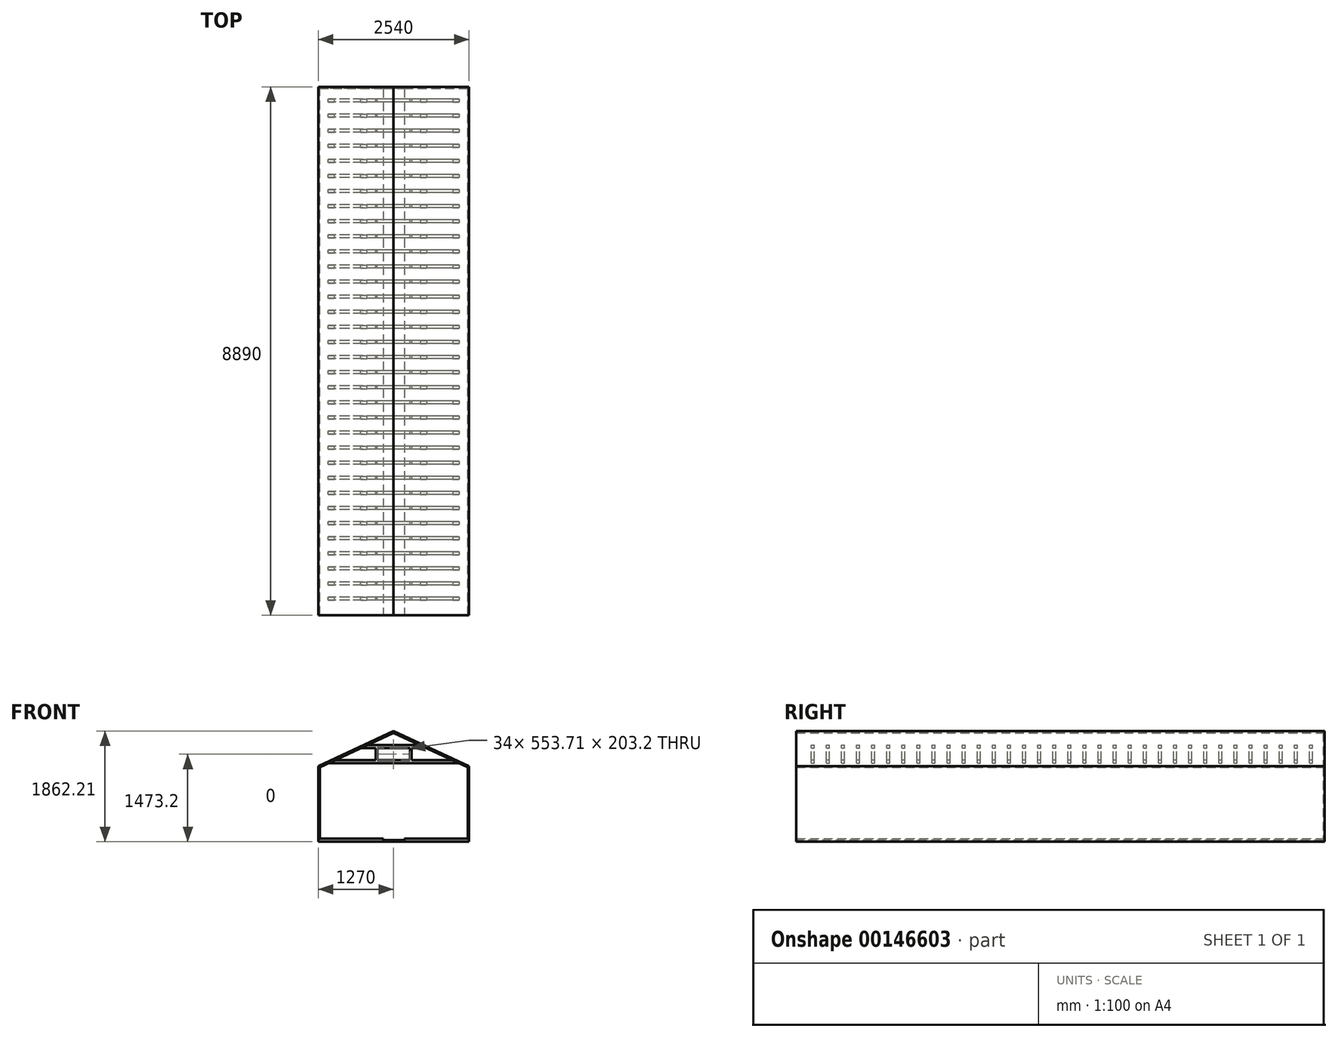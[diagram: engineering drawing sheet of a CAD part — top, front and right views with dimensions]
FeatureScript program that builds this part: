
annotation { "Feature Type Name" : "Feature", "Feature Type Description" : "" }
export const myFeature = defineFeature(function(context is Context, id is Id, definition is map)
    precondition{}
    {
        {
            var Q0;
            Q0=qCreatedBy(makeId("Front.planeOp"),FACE);
            var sketch = newSketch(context, id + "F0", { "sketchPlane" : qUnion([Q0])});
            skLineSegment(sketch, "E0", {"start": v(-1270, 1270) * mm, "end": v(-1270, 0) * mm});
            skLineSegment(sketch, "E1", {"start": v(-1270, 0) * mm, "end": v(1270, 0) * mm});
            skLineSegment(sketch, "E2", {"start": v(1270, 0) * mm, "end": v(1270, 1270) * mm});
            skLineSegment(sketch, "E3", {"start": v(1270, 1270) * mm, "end": v(0, 1862.21) * mm});
            skLineSegment(sketch, "E4", {"start": v(0, 1862.21) * mm, "end": v(-1270, 1270) * mm});
            skSolve(sketch);
        }
        {
            var Q0;
            Q0 = qSketchRegion(id + "F0", true);
            extrude(context, id + "F1", {"entities" : qUnion([Q0]), "depth" : 8890 * mm});
        }
        {
            var Q0;
            Q0=makeQuery(id+"F1.opExtrude","CAP_FACE",FACE,{"disambiguationData":[OSD([sQuery(id+"F0.wireOp",EDGE,"E0"),sQuery(id+"F0.wireOp",EDGE,"E1"),sQuery(id+"F0.wireOp",EDGE,"E2"),sQuery(id+"F0.wireOp",EDGE,"E3"),sQuery(id+"F0.wireOp",EDGE,"E4")])],"isStart":false});
            shell(context, id + "F2", {"entities" : qUnion([Q0]), "thickness" : 25.4 * mm});
        }
        {
            var Q0;
            Q0=makeQuery(id+"F2.opShell","OFFSET_FACE",FACE,{"disambiguationData":[OSD([sQuery(id+"F0.wireOp",EDGE,"E1")])]});
            var sketch = newSketch(context, id + "F3", { "sketchPlane" : qUnion([Q0])});
            skLineSegment(sketch, "E5.bottom", {"start": v(-1244.6, -25.4) * mm, "end": v(1244.6, -25.4) * mm});
            skLineSegment(sketch, "E5.top", {"start": v(-1244.6, -8890) * mm, "end": v(1244.6, -8890) * mm});
            skLineSegment(sketch, "E5.left", {"start": v(-1244.6, -25.4) * mm, "end": v(-1244.6, -8890) * mm});
            skLineSegment(sketch, "E5.right", {"start": v(1244.6, -25.4) * mm, "end": v(1244.6, -8890) * mm});
            skLineSegment(sketch, "E6.bottom", {"start": v(-152.4, -25.4) * mm, "end": v(152.4, -25.4) * mm});
            skLineSegment(sketch, "E6.top", {"start": v(-152.4, -8890) * mm, "end": v(152.4, -8890) * mm});
            skLineSegment(sketch, "E6.left", {"start": v(-152.4, -25.4) * mm, "end": v(-152.4, -8890) * mm});
            skLineSegment(sketch, "E6.right", {"start": v(152.4, -25.4) * mm, "end": v(152.4, -8890) * mm});
            skLineSegment(sketch, "E7", {"start": v(-177.8, 0) * mm, "end": v(-177.8, -8890) * mm});
            skLineSegment(sketch, "E8", {"start": v(-177.8, -8890) * mm, "end": v(-152.4, -8890) * mm});
            skLineSegment(sketch, "E9", {"start": v(-177.8, 0) * mm, "end": v(-152.4, 0) * mm});
            skLineSegment(sketch, "E10", {"start": v(-152.4, 0) * mm, "end": v(-152.4, -25.4) * mm});
            skLineSegment(sketch, "E11", {"start": v(152.4, -25.4) * mm, "end": v(152.4, 0) * mm});
            skLineSegment(sketch, "E12", {"start": v(152.4, 0) * mm, "end": v(177.8, 0) * mm});
            skLineSegment(sketch, "E13", {"start": v(177.8, 0) * mm, "end": v(177.8, -8890) * mm});
            skLineSegment(sketch, "E14", {"start": v(152.4, -8890) * mm, "end": v(177.8, -8890) * mm});
            skSolve(sketch);
        }
        {
            var Q0;
            {var subQ0=sQuery(id+"F3.wireOp",EDGE,"E5.left");Q0=makeQuery(id+"F3.imprint","IMPRINT",FACE,{"disambiguationData":[TD([[makeQuery(id+"F3.imprint","IMPRINT",EDGE,{"derivedFrom":subQ0}),-1.0]])]});}
            var Q1;
            {var subQ4=sQuery(id+"F3.wireOp",EDGE,"E9");Q1=makeQuery(id+"F3.imprint","IMPRINT",FACE,{"disambiguationData":[TD([[makeQuery(id+"F3.imprint","IMPRINT",EDGE,{"derivedFrom":subQ4}),-1.0]])]});}
            var Q2;
            {var subQ0=sQuery(id+"F3.wireOp",EDGE,"E11");Q2=makeQuery(id+"F3.imprint","IMPRINT",FACE,{"disambiguationData":[TD([[makeQuery(id+"F3.imprint","IMPRINT",EDGE,{"derivedFrom":subQ0}),-1.0]])]});}
            var Q3;
            {var subQ0=sQuery(id+"F3.wireOp",EDGE,"E5.right");Q3=makeQuery(id+"F3.imprint","IMPRINT",FACE,{"disambiguationData":[TD([[makeQuery(id+"F3.imprint","IMPRINT",EDGE,{"derivedFrom":subQ0}),1.0]])]});}
            var Q4;
            Q4=makeQuery(id+"F3.imprint","IMPRINT",FACE,{"disambiguationData":[TD([[makeQuery(id+"F3.imprint","IMPRINT",EDGE,{"derivedFrom":sQuery(id+"F3.wireOp",EDGE,"E6.bottom")}),-1.0]])]});
            extrude(context, id + "F4", {"entities" : qUnion([Q0, Q1, Q2, Q3, Q4]), "operationType" : NewBodyOperationType.ADD, "depth" : 25.4 * mm});
        }
        {
            var Q0;
            Q0=qCreatedBy(makeId("Right.planeOp"),FACE);
            var sketch = newSketch(context, id + "F5", { "sketchPlane" : qUnion([Q0])});
            skLineSegment(sketch, "E15.bottom", {"start": v(-8636, 1320.8) * mm, "end": v(-8585.2, 1320.8) * mm});
            skLineSegment(sketch, "E15.top", {"start": v(-8636, 1371.6) * mm, "end": v(-8585.2, 1371.6) * mm});
            skLineSegment(sketch, "E15.left", {"start": v(-8636, 1320.8) * mm, "end": v(-8636, 1371.6) * mm});
            skLineSegment(sketch, "E15.right", {"start": v(-8585.2, 1320.8) * mm, "end": v(-8585.2, 1371.6) * mm});
            skLineSegment(sketch, "E16.0.1.0", {"start": v(-8636, 1625.6) * mm, "end": v(-8585.2, 1625.6) * mm});
            skLineSegment(sketch, "E16.0.1.1", {"start": v(-8585.2, 1574.8) * mm, "end": v(-8585.2, 1625.6) * mm});
            skLineSegment(sketch, "E16.0.1.2", {"start": v(-8636, 1574.8) * mm, "end": v(-8585.2, 1574.8) * mm});
            skLineSegment(sketch, "E16.0.1.3", {"start": v(-8636, 1574.8) * mm, "end": v(-8636, 1625.6) * mm});
            skLineSegment(sketch, "E16.1.0.0", {"start": v(-8382, 1371.6) * mm, "end": v(-8331.2, 1371.6) * mm});
            skLineSegment(sketch, "E16.1.0.1", {"start": v(-8331.2, 1320.8) * mm, "end": v(-8331.2, 1371.6) * mm});
            skLineSegment(sketch, "E16.1.0.2", {"start": v(-8382, 1320.8) * mm, "end": v(-8331.2, 1320.8) * mm});
            skLineSegment(sketch, "E16.1.0.3", {"start": v(-8382, 1320.8) * mm, "end": v(-8382, 1371.6) * mm});
            skLineSegment(sketch, "E16.1.1.0", {"start": v(-8382, 1625.6) * mm, "end": v(-8331.2, 1625.6) * mm});
            skLineSegment(sketch, "E16.1.1.1", {"start": v(-8331.2, 1574.8) * mm, "end": v(-8331.2, 1625.6) * mm});
            skLineSegment(sketch, "E16.1.1.2", {"start": v(-8382, 1574.8) * mm, "end": v(-8331.2, 1574.8) * mm});
            skLineSegment(sketch, "E16.1.1.3", {"start": v(-8382, 1574.8) * mm, "end": v(-8382, 1625.6) * mm});
            skLineSegment(sketch, "E16.2.0.0", {"start": v(-8128, 1371.6) * mm, "end": v(-8077.2, 1371.6) * mm});
            skLineSegment(sketch, "E16.2.0.1", {"start": v(-8077.2, 1320.8) * mm, "end": v(-8077.2, 1371.6) * mm});
            skLineSegment(sketch, "E16.2.0.2", {"start": v(-8128, 1320.8) * mm, "end": v(-8077.2, 1320.8) * mm});
            skLineSegment(sketch, "E16.2.0.3", {"start": v(-8128, 1320.8) * mm, "end": v(-8128, 1371.6) * mm});
            skLineSegment(sketch, "E16.2.1.0", {"start": v(-8128, 1625.6) * mm, "end": v(-8077.2, 1625.6) * mm});
            skLineSegment(sketch, "E16.2.1.1", {"start": v(-8077.2, 1574.8) * mm, "end": v(-8077.2, 1625.6) * mm});
            skLineSegment(sketch, "E16.2.1.2", {"start": v(-8128, 1574.8) * mm, "end": v(-8077.2, 1574.8) * mm});
            skLineSegment(sketch, "E16.2.1.3", {"start": v(-8128, 1574.8) * mm, "end": v(-8128, 1625.6) * mm});
            skLineSegment(sketch, "E16.3.0.0", {"start": v(-7874, 1371.6) * mm, "end": v(-7823.2, 1371.6) * mm});
            skLineSegment(sketch, "E16.3.0.1", {"start": v(-7823.2, 1320.8) * mm, "end": v(-7823.2, 1371.6) * mm});
            skLineSegment(sketch, "E16.3.0.2", {"start": v(-7874, 1320.8) * mm, "end": v(-7823.2, 1320.8) * mm});
            skLineSegment(sketch, "E16.3.0.3", {"start": v(-7874, 1320.8) * mm, "end": v(-7874, 1371.6) * mm});
            skLineSegment(sketch, "E16.3.1.0", {"start": v(-7874, 1625.6) * mm, "end": v(-7823.2, 1625.6) * mm});
            skLineSegment(sketch, "E16.3.1.1", {"start": v(-7823.2, 1574.8) * mm, "end": v(-7823.2, 1625.6) * mm});
            skLineSegment(sketch, "E16.3.1.2", {"start": v(-7874, 1574.8) * mm, "end": v(-7823.2, 1574.8) * mm});
            skLineSegment(sketch, "E16.3.1.3", {"start": v(-7874, 1574.8) * mm, "end": v(-7874, 1625.6) * mm});
            skLineSegment(sketch, "E16.4.0.0", {"start": v(-7620, 1371.6) * mm, "end": v(-7569.2, 1371.6) * mm});
            skLineSegment(sketch, "E16.4.0.1", {"start": v(-7569.2, 1320.8) * mm, "end": v(-7569.2, 1371.6) * mm});
            skLineSegment(sketch, "E16.4.0.2", {"start": v(-7620, 1320.8) * mm, "end": v(-7569.2, 1320.8) * mm});
            skLineSegment(sketch, "E16.4.0.3", {"start": v(-7620, 1320.8) * mm, "end": v(-7620, 1371.6) * mm});
            skLineSegment(sketch, "E16.4.1.0", {"start": v(-7620, 1625.6) * mm, "end": v(-7569.2, 1625.6) * mm});
            skLineSegment(sketch, "E16.4.1.1", {"start": v(-7569.2, 1574.8) * mm, "end": v(-7569.2, 1625.6) * mm});
            skLineSegment(sketch, "E16.4.1.2", {"start": v(-7620, 1574.8) * mm, "end": v(-7569.2, 1574.8) * mm});
            skLineSegment(sketch, "E16.4.1.3", {"start": v(-7620, 1574.8) * mm, "end": v(-7620, 1625.6) * mm});
            skLineSegment(sketch, "E16.5.0.0", {"start": v(-7366, 1371.6) * mm, "end": v(-7315.2, 1371.6) * mm});
            skLineSegment(sketch, "E16.5.0.1", {"start": v(-7315.2, 1320.8) * mm, "end": v(-7315.2, 1371.6) * mm});
            skLineSegment(sketch, "E16.5.0.2", {"start": v(-7366, 1320.8) * mm, "end": v(-7315.2, 1320.8) * mm});
            skLineSegment(sketch, "E16.5.0.3", {"start": v(-7366, 1320.8) * mm, "end": v(-7366, 1371.6) * mm});
            skLineSegment(sketch, "E16.5.1.0", {"start": v(-7366, 1625.6) * mm, "end": v(-7315.2, 1625.6) * mm});
            skLineSegment(sketch, "E16.5.1.1", {"start": v(-7315.2, 1574.8) * mm, "end": v(-7315.2, 1625.6) * mm});
            skLineSegment(sketch, "E16.5.1.2", {"start": v(-7366, 1574.8) * mm, "end": v(-7315.2, 1574.8) * mm});
            skLineSegment(sketch, "E16.5.1.3", {"start": v(-7366, 1574.8) * mm, "end": v(-7366, 1625.6) * mm});
            skLineSegment(sketch, "E16.6.0.0", {"start": v(-7112, 1371.6) * mm, "end": v(-7061.2, 1371.6) * mm});
            skLineSegment(sketch, "E16.6.0.1", {"start": v(-7061.2, 1320.8) * mm, "end": v(-7061.2, 1371.6) * mm});
            skLineSegment(sketch, "E16.6.0.2", {"start": v(-7112, 1320.8) * mm, "end": v(-7061.2, 1320.8) * mm});
            skLineSegment(sketch, "E16.6.0.3", {"start": v(-7112, 1320.8) * mm, "end": v(-7112, 1371.6) * mm});
            skLineSegment(sketch, "E16.6.1.0", {"start": v(-7112, 1625.6) * mm, "end": v(-7061.2, 1625.6) * mm});
            skLineSegment(sketch, "E16.6.1.1", {"start": v(-7061.2, 1574.8) * mm, "end": v(-7061.2, 1625.6) * mm});
            skLineSegment(sketch, "E16.6.1.2", {"start": v(-7112, 1574.8) * mm, "end": v(-7061.2, 1574.8) * mm});
            skLineSegment(sketch, "E16.6.1.3", {"start": v(-7112, 1574.8) * mm, "end": v(-7112, 1625.6) * mm});
            skLineSegment(sketch, "E16.7.0.0", {"start": v(-6858, 1371.6) * mm, "end": v(-6807.2, 1371.6) * mm});
            skLineSegment(sketch, "E16.7.0.1", {"start": v(-6807.2, 1320.8) * mm, "end": v(-6807.2, 1371.6) * mm});
            skLineSegment(sketch, "E16.7.0.2", {"start": v(-6858, 1320.8) * mm, "end": v(-6807.2, 1320.8) * mm});
            skLineSegment(sketch, "E16.7.0.3", {"start": v(-6858, 1320.8) * mm, "end": v(-6858, 1371.6) * mm});
            skLineSegment(sketch, "E16.7.1.0", {"start": v(-6858, 1625.6) * mm, "end": v(-6807.2, 1625.6) * mm});
            skLineSegment(sketch, "E16.7.1.1", {"start": v(-6807.2, 1574.8) * mm, "end": v(-6807.2, 1625.6) * mm});
            skLineSegment(sketch, "E16.7.1.2", {"start": v(-6858, 1574.8) * mm, "end": v(-6807.2, 1574.8) * mm});
            skLineSegment(sketch, "E16.7.1.3", {"start": v(-6858, 1574.8) * mm, "end": v(-6858, 1625.6) * mm});
            skLineSegment(sketch, "E16.8.0.0", {"start": v(-6604, 1371.6) * mm, "end": v(-6553.2, 1371.6) * mm});
            skLineSegment(sketch, "E16.8.0.1", {"start": v(-6553.2, 1320.8) * mm, "end": v(-6553.2, 1371.6) * mm});
            skLineSegment(sketch, "E16.8.0.2", {"start": v(-6604, 1320.8) * mm, "end": v(-6553.2, 1320.8) * mm});
            skLineSegment(sketch, "E16.8.0.3", {"start": v(-6604, 1320.8) * mm, "end": v(-6604, 1371.6) * mm});
            skLineSegment(sketch, "E16.8.1.0", {"start": v(-6604, 1625.6) * mm, "end": v(-6553.2, 1625.6) * mm});
            skLineSegment(sketch, "E16.8.1.1", {"start": v(-6553.2, 1574.8) * mm, "end": v(-6553.2, 1625.6) * mm});
            skLineSegment(sketch, "E16.8.1.2", {"start": v(-6604, 1574.8) * mm, "end": v(-6553.2, 1574.8) * mm});
            skLineSegment(sketch, "E16.8.1.3", {"start": v(-6604, 1574.8) * mm, "end": v(-6604, 1625.6) * mm});
            skLineSegment(sketch, "E16.9.0.0", {"start": v(-6350, 1371.6) * mm, "end": v(-6299.2, 1371.6) * mm});
            skLineSegment(sketch, "E16.9.0.1", {"start": v(-6299.2, 1320.8) * mm, "end": v(-6299.2, 1371.6) * mm});
            skLineSegment(sketch, "E16.9.0.2", {"start": v(-6350, 1320.8) * mm, "end": v(-6299.2, 1320.8) * mm});
            skLineSegment(sketch, "E16.9.0.3", {"start": v(-6350, 1320.8) * mm, "end": v(-6350, 1371.6) * mm});
            skLineSegment(sketch, "E16.9.1.0", {"start": v(-6350, 1625.6) * mm, "end": v(-6299.2, 1625.6) * mm});
            skLineSegment(sketch, "E16.9.1.1", {"start": v(-6299.2, 1574.8) * mm, "end": v(-6299.2, 1625.6) * mm});
            skLineSegment(sketch, "E16.9.1.2", {"start": v(-6350, 1574.8) * mm, "end": v(-6299.2, 1574.8) * mm});
            skLineSegment(sketch, "E16.9.1.3", {"start": v(-6350, 1574.8) * mm, "end": v(-6350, 1625.6) * mm});
            skLineSegment(sketch, "E16.10.0.0", {"start": v(-6096, 1371.6) * mm, "end": v(-6045.2, 1371.6) * mm});
            skLineSegment(sketch, "E16.10.0.1", {"start": v(-6045.2, 1320.8) * mm, "end": v(-6045.2, 1371.6) * mm});
            skLineSegment(sketch, "E16.10.0.2", {"start": v(-6096, 1320.8) * mm, "end": v(-6045.2, 1320.8) * mm});
            skLineSegment(sketch, "E16.10.0.3", {"start": v(-6096, 1320.8) * mm, "end": v(-6096, 1371.6) * mm});
            skLineSegment(sketch, "E16.10.1.0", {"start": v(-6096, 1625.6) * mm, "end": v(-6045.2, 1625.6) * mm});
            skLineSegment(sketch, "E16.10.1.1", {"start": v(-6045.2, 1574.8) * mm, "end": v(-6045.2, 1625.6) * mm});
            skLineSegment(sketch, "E16.10.1.2", {"start": v(-6096, 1574.8) * mm, "end": v(-6045.2, 1574.8) * mm});
            skLineSegment(sketch, "E16.10.1.3", {"start": v(-6096, 1574.8) * mm, "end": v(-6096, 1625.6) * mm});
            skLineSegment(sketch, "E16.11.0.0", {"start": v(-5842, 1371.6) * mm, "end": v(-5791.2, 1371.6) * mm});
            skLineSegment(sketch, "E16.11.0.1", {"start": v(-5791.2, 1320.8) * mm, "end": v(-5791.2, 1371.6) * mm});
            skLineSegment(sketch, "E16.11.0.2", {"start": v(-5842, 1320.8) * mm, "end": v(-5791.2, 1320.8) * mm});
            skLineSegment(sketch, "E16.11.0.3", {"start": v(-5842, 1320.8) * mm, "end": v(-5842, 1371.6) * mm});
            skLineSegment(sketch, "E16.11.1.0", {"start": v(-5842, 1625.6) * mm, "end": v(-5791.2, 1625.6) * mm});
            skLineSegment(sketch, "E16.11.1.1", {"start": v(-5791.2, 1574.8) * mm, "end": v(-5791.2, 1625.6) * mm});
            skLineSegment(sketch, "E16.11.1.2", {"start": v(-5842, 1574.8) * mm, "end": v(-5791.2, 1574.8) * mm});
            skLineSegment(sketch, "E16.11.1.3", {"start": v(-5842, 1574.8) * mm, "end": v(-5842, 1625.6) * mm});
            skLineSegment(sketch, "E16.12.0.0", {"start": v(-5588, 1371.6) * mm, "end": v(-5537.2, 1371.6) * mm});
            skLineSegment(sketch, "E16.12.0.1", {"start": v(-5537.2, 1320.8) * mm, "end": v(-5537.2, 1371.6) * mm});
            skLineSegment(sketch, "E16.12.0.2", {"start": v(-5588, 1320.8) * mm, "end": v(-5537.2, 1320.8) * mm});
            skLineSegment(sketch, "E16.12.0.3", {"start": v(-5588, 1320.8) * mm, "end": v(-5588, 1371.6) * mm});
            skLineSegment(sketch, "E16.12.1.0", {"start": v(-5588, 1625.6) * mm, "end": v(-5537.2, 1625.6) * mm});
            skLineSegment(sketch, "E16.12.1.1", {"start": v(-5537.2, 1574.8) * mm, "end": v(-5537.2, 1625.6) * mm});
            skLineSegment(sketch, "E16.12.1.2", {"start": v(-5588, 1574.8) * mm, "end": v(-5537.2, 1574.8) * mm});
            skLineSegment(sketch, "E16.12.1.3", {"start": v(-5588, 1574.8) * mm, "end": v(-5588, 1625.6) * mm});
            skLineSegment(sketch, "E16.13.0.0", {"start": v(-5334, 1371.6) * mm, "end": v(-5283.2, 1371.6) * mm});
            skLineSegment(sketch, "E16.13.0.1", {"start": v(-5283.2, 1320.8) * mm, "end": v(-5283.2, 1371.6) * mm});
            skLineSegment(sketch, "E16.13.0.2", {"start": v(-5334, 1320.8) * mm, "end": v(-5283.2, 1320.8) * mm});
            skLineSegment(sketch, "E16.13.0.3", {"start": v(-5334, 1320.8) * mm, "end": v(-5334, 1371.6) * mm});
            skLineSegment(sketch, "E16.13.1.0", {"start": v(-5334, 1625.6) * mm, "end": v(-5283.2, 1625.6) * mm});
            skLineSegment(sketch, "E16.13.1.1", {"start": v(-5283.2, 1574.8) * mm, "end": v(-5283.2, 1625.6) * mm});
            skLineSegment(sketch, "E16.13.1.2", {"start": v(-5334, 1574.8) * mm, "end": v(-5283.2, 1574.8) * mm});
            skLineSegment(sketch, "E16.13.1.3", {"start": v(-5334, 1574.8) * mm, "end": v(-5334, 1625.6) * mm});
            skLineSegment(sketch, "E16.14.0.0", {"start": v(-5080, 1371.6) * mm, "end": v(-5029.2, 1371.6) * mm});
            skLineSegment(sketch, "E16.14.0.1", {"start": v(-5029.2, 1320.8) * mm, "end": v(-5029.2, 1371.6) * mm});
            skLineSegment(sketch, "E16.14.0.2", {"start": v(-5080, 1320.8) * mm, "end": v(-5029.2, 1320.8) * mm});
            skLineSegment(sketch, "E16.14.0.3", {"start": v(-5080, 1320.8) * mm, "end": v(-5080, 1371.6) * mm});
            skLineSegment(sketch, "E16.14.1.0", {"start": v(-5080, 1625.6) * mm, "end": v(-5029.2, 1625.6) * mm});
            skLineSegment(sketch, "E16.14.1.1", {"start": v(-5029.2, 1574.8) * mm, "end": v(-5029.2, 1625.6) * mm});
            skLineSegment(sketch, "E16.14.1.2", {"start": v(-5080, 1574.8) * mm, "end": v(-5029.2, 1574.8) * mm});
            skLineSegment(sketch, "E16.14.1.3", {"start": v(-5080, 1574.8) * mm, "end": v(-5080, 1625.6) * mm});
            skLineSegment(sketch, "E16.15.0.0", {"start": v(-4826, 1371.6) * mm, "end": v(-4775.2, 1371.6) * mm});
            skLineSegment(sketch, "E16.15.0.1", {"start": v(-4775.2, 1320.8) * mm, "end": v(-4775.2, 1371.6) * mm});
            skLineSegment(sketch, "E16.15.0.2", {"start": v(-4826, 1320.8) * mm, "end": v(-4775.2, 1320.8) * mm});
            skLineSegment(sketch, "E16.15.0.3", {"start": v(-4826, 1320.8) * mm, "end": v(-4826, 1371.6) * mm});
            skLineSegment(sketch, "E16.15.1.0", {"start": v(-4826, 1625.6) * mm, "end": v(-4775.2, 1625.6) * mm});
            skLineSegment(sketch, "E16.15.1.1", {"start": v(-4775.2, 1574.8) * mm, "end": v(-4775.2, 1625.6) * mm});
            skLineSegment(sketch, "E16.15.1.2", {"start": v(-4826, 1574.8) * mm, "end": v(-4775.2, 1574.8) * mm});
            skLineSegment(sketch, "E16.15.1.3", {"start": v(-4826, 1574.8) * mm, "end": v(-4826, 1625.6) * mm});
            skLineSegment(sketch, "E16.16.0.0", {"start": v(-4572, 1371.6) * mm, "end": v(-4521.2, 1371.6) * mm});
            skLineSegment(sketch, "E16.16.0.1", {"start": v(-4521.2, 1320.8) * mm, "end": v(-4521.2, 1371.6) * mm});
            skLineSegment(sketch, "E16.16.0.2", {"start": v(-4572, 1320.8) * mm, "end": v(-4521.2, 1320.8) * mm});
            skLineSegment(sketch, "E16.16.0.3", {"start": v(-4572, 1320.8) * mm, "end": v(-4572, 1371.6) * mm});
            skLineSegment(sketch, "E16.16.1.0", {"start": v(-4572, 1625.6) * mm, "end": v(-4521.2, 1625.6) * mm});
            skLineSegment(sketch, "E16.16.1.1", {"start": v(-4521.2, 1574.8) * mm, "end": v(-4521.2, 1625.6) * mm});
            skLineSegment(sketch, "E16.16.1.2", {"start": v(-4572, 1574.8) * mm, "end": v(-4521.2, 1574.8) * mm});
            skLineSegment(sketch, "E16.16.1.3", {"start": v(-4572, 1574.8) * mm, "end": v(-4572, 1625.6) * mm});
            skLineSegment(sketch, "E16.17.0.0", {"start": v(-4318, 1371.6) * mm, "end": v(-4267.2, 1371.6) * mm});
            skLineSegment(sketch, "E16.17.0.1", {"start": v(-4267.2, 1320.8) * mm, "end": v(-4267.2, 1371.6) * mm});
            skLineSegment(sketch, "E16.17.0.2", {"start": v(-4318, 1320.8) * mm, "end": v(-4267.2, 1320.8) * mm});
            skLineSegment(sketch, "E16.17.0.3", {"start": v(-4318, 1320.8) * mm, "end": v(-4318, 1371.6) * mm});
            skLineSegment(sketch, "E16.17.1.0", {"start": v(-4318, 1625.6) * mm, "end": v(-4267.2, 1625.6) * mm});
            skLineSegment(sketch, "E16.17.1.1", {"start": v(-4267.2, 1574.8) * mm, "end": v(-4267.2, 1625.6) * mm});
            skLineSegment(sketch, "E16.17.1.2", {"start": v(-4318, 1574.8) * mm, "end": v(-4267.2, 1574.8) * mm});
            skLineSegment(sketch, "E16.17.1.3", {"start": v(-4318, 1574.8) * mm, "end": v(-4318, 1625.6) * mm});
            skLineSegment(sketch, "E16.18.0.0", {"start": v(-4064, 1371.6) * mm, "end": v(-4013.2, 1371.6) * mm});
            skLineSegment(sketch, "E16.18.0.1", {"start": v(-4013.2, 1320.8) * mm, "end": v(-4013.2, 1371.6) * mm});
            skLineSegment(sketch, "E16.18.0.2", {"start": v(-4064, 1320.8) * mm, "end": v(-4013.2, 1320.8) * mm});
            skLineSegment(sketch, "E16.18.0.3", {"start": v(-4064, 1320.8) * mm, "end": v(-4064, 1371.6) * mm});
            skLineSegment(sketch, "E16.18.1.0", {"start": v(-4064, 1625.6) * mm, "end": v(-4013.2, 1625.6) * mm});
            skLineSegment(sketch, "E16.18.1.1", {"start": v(-4013.2, 1574.8) * mm, "end": v(-4013.2, 1625.6) * mm});
            skLineSegment(sketch, "E16.18.1.2", {"start": v(-4064, 1574.8) * mm, "end": v(-4013.2, 1574.8) * mm});
            skLineSegment(sketch, "E16.18.1.3", {"start": v(-4064, 1574.8) * mm, "end": v(-4064, 1625.6) * mm});
            skLineSegment(sketch, "E16.19.0.0", {"start": v(-3810, 1371.6) * mm, "end": v(-3759.2, 1371.6) * mm});
            skLineSegment(sketch, "E16.19.0.1", {"start": v(-3759.2, 1320.8) * mm, "end": v(-3759.2, 1371.6) * mm});
            skLineSegment(sketch, "E16.19.0.2", {"start": v(-3810, 1320.8) * mm, "end": v(-3759.2, 1320.8) * mm});
            skLineSegment(sketch, "E16.19.0.3", {"start": v(-3810, 1320.8) * mm, "end": v(-3810, 1371.6) * mm});
            skLineSegment(sketch, "E16.19.1.0", {"start": v(-3810, 1625.6) * mm, "end": v(-3759.2, 1625.6) * mm});
            skLineSegment(sketch, "E16.19.1.1", {"start": v(-3759.2, 1574.8) * mm, "end": v(-3759.2, 1625.6) * mm});
            skLineSegment(sketch, "E16.19.1.2", {"start": v(-3810, 1574.8) * mm, "end": v(-3759.2, 1574.8) * mm});
            skLineSegment(sketch, "E16.19.1.3", {"start": v(-3810, 1574.8) * mm, "end": v(-3810, 1625.6) * mm});
            skLineSegment(sketch, "E16.20.0.0", {"start": v(-3556, 1371.6) * mm, "end": v(-3505.2, 1371.6) * mm});
            skLineSegment(sketch, "E16.20.0.1", {"start": v(-3505.2, 1320.8) * mm, "end": v(-3505.2, 1371.6) * mm});
            skLineSegment(sketch, "E16.20.0.2", {"start": v(-3556, 1320.8) * mm, "end": v(-3505.2, 1320.8) * mm});
            skLineSegment(sketch, "E16.20.0.3", {"start": v(-3556, 1320.8) * mm, "end": v(-3556, 1371.6) * mm});
            skLineSegment(sketch, "E16.20.1.0", {"start": v(-3556, 1625.6) * mm, "end": v(-3505.2, 1625.6) * mm});
            skLineSegment(sketch, "E16.20.1.1", {"start": v(-3505.2, 1574.8) * mm, "end": v(-3505.2, 1625.6) * mm});
            skLineSegment(sketch, "E16.20.1.2", {"start": v(-3556, 1574.8) * mm, "end": v(-3505.2, 1574.8) * mm});
            skLineSegment(sketch, "E16.20.1.3", {"start": v(-3556, 1574.8) * mm, "end": v(-3556, 1625.6) * mm});
            skLineSegment(sketch, "E16.21.0.0", {"start": v(-3302, 1371.6) * mm, "end": v(-3251.2, 1371.6) * mm});
            skLineSegment(sketch, "E16.21.0.1", {"start": v(-3251.2, 1320.8) * mm, "end": v(-3251.2, 1371.6) * mm});
            skLineSegment(sketch, "E16.21.0.2", {"start": v(-3302, 1320.8) * mm, "end": v(-3251.2, 1320.8) * mm});
            skLineSegment(sketch, "E16.21.0.3", {"start": v(-3302, 1320.8) * mm, "end": v(-3302, 1371.6) * mm});
            skLineSegment(sketch, "E16.21.1.0", {"start": v(-3302, 1625.6) * mm, "end": v(-3251.2, 1625.6) * mm});
            skLineSegment(sketch, "E16.21.1.1", {"start": v(-3251.2, 1574.8) * mm, "end": v(-3251.2, 1625.6) * mm});
            skLineSegment(sketch, "E16.21.1.2", {"start": v(-3302, 1574.8) * mm, "end": v(-3251.2, 1574.8) * mm});
            skLineSegment(sketch, "E16.21.1.3", {"start": v(-3302, 1574.8) * mm, "end": v(-3302, 1625.6) * mm});
            skLineSegment(sketch, "E16.22.0.0", {"start": v(-3048, 1371.6) * mm, "end": v(-2997.2, 1371.6) * mm});
            skLineSegment(sketch, "E16.22.0.1", {"start": v(-2997.2, 1320.8) * mm, "end": v(-2997.2, 1371.6) * mm});
            skLineSegment(sketch, "E16.22.0.2", {"start": v(-3048, 1320.8) * mm, "end": v(-2997.2, 1320.8) * mm});
            skLineSegment(sketch, "E16.22.0.3", {"start": v(-3048, 1320.8) * mm, "end": v(-3048, 1371.6) * mm});
            skLineSegment(sketch, "E16.22.1.0", {"start": v(-3048, 1625.6) * mm, "end": v(-2997.2, 1625.6) * mm});
            skLineSegment(sketch, "E16.22.1.1", {"start": v(-2997.2, 1574.8) * mm, "end": v(-2997.2, 1625.6) * mm});
            skLineSegment(sketch, "E16.22.1.2", {"start": v(-3048, 1574.8) * mm, "end": v(-2997.2, 1574.8) * mm});
            skLineSegment(sketch, "E16.22.1.3", {"start": v(-3048, 1574.8) * mm, "end": v(-3048, 1625.6) * mm});
            skLineSegment(sketch, "E16.23.0.0", {"start": v(-2794, 1371.6) * mm, "end": v(-2743.2, 1371.6) * mm});
            skLineSegment(sketch, "E16.23.0.1", {"start": v(-2743.2, 1320.8) * mm, "end": v(-2743.2, 1371.6) * mm});
            skLineSegment(sketch, "E16.23.0.2", {"start": v(-2794, 1320.8) * mm, "end": v(-2743.2, 1320.8) * mm});
            skLineSegment(sketch, "E16.23.0.3", {"start": v(-2794, 1320.8) * mm, "end": v(-2794, 1371.6) * mm});
            skLineSegment(sketch, "E16.23.1.0", {"start": v(-2794, 1625.6) * mm, "end": v(-2743.2, 1625.6) * mm});
            skLineSegment(sketch, "E16.23.1.1", {"start": v(-2743.2, 1574.8) * mm, "end": v(-2743.2, 1625.6) * mm});
            skLineSegment(sketch, "E16.23.1.2", {"start": v(-2794, 1574.8) * mm, "end": v(-2743.2, 1574.8) * mm});
            skLineSegment(sketch, "E16.23.1.3", {"start": v(-2794, 1574.8) * mm, "end": v(-2794, 1625.6) * mm});
            skLineSegment(sketch, "E16.24.0.0", {"start": v(-2540, 1371.6) * mm, "end": v(-2489.2, 1371.6) * mm});
            skLineSegment(sketch, "E16.24.0.1", {"start": v(-2489.2, 1320.8) * mm, "end": v(-2489.2, 1371.6) * mm});
            skLineSegment(sketch, "E16.24.0.2", {"start": v(-2540, 1320.8) * mm, "end": v(-2489.2, 1320.8) * mm});
            skLineSegment(sketch, "E16.24.0.3", {"start": v(-2540, 1320.8) * mm, "end": v(-2540, 1371.6) * mm});
            skLineSegment(sketch, "E16.24.1.0", {"start": v(-2540, 1625.6) * mm, "end": v(-2489.2, 1625.6) * mm});
            skLineSegment(sketch, "E16.24.1.1", {"start": v(-2489.2, 1574.8) * mm, "end": v(-2489.2, 1625.6) * mm});
            skLineSegment(sketch, "E16.24.1.2", {"start": v(-2540, 1574.8) * mm, "end": v(-2489.2, 1574.8) * mm});
            skLineSegment(sketch, "E16.24.1.3", {"start": v(-2540, 1574.8) * mm, "end": v(-2540, 1625.6) * mm});
            skLineSegment(sketch, "E16.25.0.0", {"start": v(-2286, 1371.6) * mm, "end": v(-2235.2, 1371.6) * mm});
            skLineSegment(sketch, "E16.25.0.1", {"start": v(-2235.2, 1320.8) * mm, "end": v(-2235.2, 1371.6) * mm});
            skLineSegment(sketch, "E16.25.0.2", {"start": v(-2286, 1320.8) * mm, "end": v(-2235.2, 1320.8) * mm});
            skLineSegment(sketch, "E16.25.0.3", {"start": v(-2286, 1320.8) * mm, "end": v(-2286, 1371.6) * mm});
            skLineSegment(sketch, "E16.25.1.0", {"start": v(-2286, 1625.6) * mm, "end": v(-2235.2, 1625.6) * mm});
            skLineSegment(sketch, "E16.25.1.1", {"start": v(-2235.2, 1574.8) * mm, "end": v(-2235.2, 1625.6) * mm});
            skLineSegment(sketch, "E16.25.1.2", {"start": v(-2286, 1574.8) * mm, "end": v(-2235.2, 1574.8) * mm});
            skLineSegment(sketch, "E16.25.1.3", {"start": v(-2286, 1574.8) * mm, "end": v(-2286, 1625.6) * mm});
            skLineSegment(sketch, "E16.26.0.0", {"start": v(-2032, 1371.6) * mm, "end": v(-1981.2, 1371.6) * mm});
            skLineSegment(sketch, "E16.26.0.1", {"start": v(-1981.2, 1320.8) * mm, "end": v(-1981.2, 1371.6) * mm});
            skLineSegment(sketch, "E16.26.0.2", {"start": v(-2032, 1320.8) * mm, "end": v(-1981.2, 1320.8) * mm});
            skLineSegment(sketch, "E16.26.0.3", {"start": v(-2032, 1320.8) * mm, "end": v(-2032, 1371.6) * mm});
            skLineSegment(sketch, "E16.26.1.0", {"start": v(-2032, 1625.6) * mm, "end": v(-1981.2, 1625.6) * mm});
            skLineSegment(sketch, "E16.26.1.1", {"start": v(-1981.2, 1574.8) * mm, "end": v(-1981.2, 1625.6) * mm});
            skLineSegment(sketch, "E16.26.1.2", {"start": v(-2032, 1574.8) * mm, "end": v(-1981.2, 1574.8) * mm});
            skLineSegment(sketch, "E16.26.1.3", {"start": v(-2032, 1574.8) * mm, "end": v(-2032, 1625.6) * mm});
            skLineSegment(sketch, "E16.27.0.0", {"start": v(-1778, 1371.6) * mm, "end": v(-1727.2, 1371.6) * mm});
            skLineSegment(sketch, "E16.27.0.1", {"start": v(-1727.2, 1320.8) * mm, "end": v(-1727.2, 1371.6) * mm});
            skLineSegment(sketch, "E16.27.0.2", {"start": v(-1778, 1320.8) * mm, "end": v(-1727.2, 1320.8) * mm});
            skLineSegment(sketch, "E16.27.0.3", {"start": v(-1778, 1320.8) * mm, "end": v(-1778, 1371.6) * mm});
            skLineSegment(sketch, "E16.27.1.0", {"start": v(-1778, 1625.6) * mm, "end": v(-1727.2, 1625.6) * mm});
            skLineSegment(sketch, "E16.27.1.1", {"start": v(-1727.2, 1574.8) * mm, "end": v(-1727.2, 1625.6) * mm});
            skLineSegment(sketch, "E16.27.1.2", {"start": v(-1778, 1574.8) * mm, "end": v(-1727.2, 1574.8) * mm});
            skLineSegment(sketch, "E16.27.1.3", {"start": v(-1778, 1574.8) * mm, "end": v(-1778, 1625.6) * mm});
            skLineSegment(sketch, "E16.28.0.0", {"start": v(-1524, 1371.6) * mm, "end": v(-1473.2, 1371.6) * mm});
            skLineSegment(sketch, "E16.28.0.1", {"start": v(-1473.2, 1320.8) * mm, "end": v(-1473.2, 1371.6) * mm});
            skLineSegment(sketch, "E16.28.0.2", {"start": v(-1524, 1320.8) * mm, "end": v(-1473.2, 1320.8) * mm});
            skLineSegment(sketch, "E16.28.0.3", {"start": v(-1524, 1320.8) * mm, "end": v(-1524, 1371.6) * mm});
            skLineSegment(sketch, "E16.28.1.0", {"start": v(-1524, 1625.6) * mm, "end": v(-1473.2, 1625.6) * mm});
            skLineSegment(sketch, "E16.28.1.1", {"start": v(-1473.2, 1574.8) * mm, "end": v(-1473.2, 1625.6) * mm});
            skLineSegment(sketch, "E16.28.1.2", {"start": v(-1524, 1574.8) * mm, "end": v(-1473.2, 1574.8) * mm});
            skLineSegment(sketch, "E16.28.1.3", {"start": v(-1524, 1574.8) * mm, "end": v(-1524, 1625.6) * mm});
            skLineSegment(sketch, "E16.29.0.0", {"start": v(-1270, 1371.6) * mm, "end": v(-1219.2, 1371.6) * mm});
            skLineSegment(sketch, "E16.29.0.1", {"start": v(-1219.2, 1320.8) * mm, "end": v(-1219.2, 1371.6) * mm});
            skLineSegment(sketch, "E16.29.0.2", {"start": v(-1270, 1320.8) * mm, "end": v(-1219.2, 1320.8) * mm});
            skLineSegment(sketch, "E16.29.0.3", {"start": v(-1270, 1320.8) * mm, "end": v(-1270, 1371.6) * mm});
            skLineSegment(sketch, "E16.29.1.0", {"start": v(-1270, 1625.6) * mm, "end": v(-1219.2, 1625.6) * mm});
            skLineSegment(sketch, "E16.29.1.1", {"start": v(-1219.2, 1574.8) * mm, "end": v(-1219.2, 1625.6) * mm});
            skLineSegment(sketch, "E16.29.1.2", {"start": v(-1270, 1574.8) * mm, "end": v(-1219.2, 1574.8) * mm});
            skLineSegment(sketch, "E16.29.1.3", {"start": v(-1270, 1574.8) * mm, "end": v(-1270, 1625.6) * mm});
            skLineSegment(sketch, "E16.30.0.0", {"start": v(-1016, 1371.6) * mm, "end": v(-965.2, 1371.6) * mm});
            skLineSegment(sketch, "E16.30.0.1", {"start": v(-965.2, 1320.8) * mm, "end": v(-965.2, 1371.6) * mm});
            skLineSegment(sketch, "E16.30.0.2", {"start": v(-1016, 1320.8) * mm, "end": v(-965.2, 1320.8) * mm});
            skLineSegment(sketch, "E16.30.0.3", {"start": v(-1016, 1320.8) * mm, "end": v(-1016, 1371.6) * mm});
            skLineSegment(sketch, "E16.30.1.0", {"start": v(-1016, 1625.6) * mm, "end": v(-965.2, 1625.6) * mm});
            skLineSegment(sketch, "E16.30.1.1", {"start": v(-965.2, 1574.8) * mm, "end": v(-965.2, 1625.6) * mm});
            skLineSegment(sketch, "E16.30.1.2", {"start": v(-1016, 1574.8) * mm, "end": v(-965.2, 1574.8) * mm});
            skLineSegment(sketch, "E16.30.1.3", {"start": v(-1016, 1574.8) * mm, "end": v(-1016, 1625.6) * mm});
            skLineSegment(sketch, "E16.31.0.0", {"start": v(-762, 1371.6) * mm, "end": v(-711.2, 1371.6) * mm});
            skLineSegment(sketch, "E16.31.0.1", {"start": v(-711.2, 1320.8) * mm, "end": v(-711.2, 1371.6) * mm});
            skLineSegment(sketch, "E16.31.0.2", {"start": v(-762, 1320.8) * mm, "end": v(-711.2, 1320.8) * mm});
            skLineSegment(sketch, "E16.31.0.3", {"start": v(-762, 1320.8) * mm, "end": v(-762, 1371.6) * mm});
            skLineSegment(sketch, "E16.31.1.0", {"start": v(-762, 1625.6) * mm, "end": v(-711.2, 1625.6) * mm});
            skLineSegment(sketch, "E16.31.1.1", {"start": v(-711.2, 1574.8) * mm, "end": v(-711.2, 1625.6) * mm});
            skLineSegment(sketch, "E16.31.1.2", {"start": v(-762, 1574.8) * mm, "end": v(-711.2, 1574.8) * mm});
            skLineSegment(sketch, "E16.31.1.3", {"start": v(-762, 1574.8) * mm, "end": v(-762, 1625.6) * mm});
            skLineSegment(sketch, "E16.32.0.0", {"start": v(-508, 1371.6) * mm, "end": v(-457.2, 1371.6) * mm});
            skLineSegment(sketch, "E16.32.0.1", {"start": v(-457.2, 1320.8) * mm, "end": v(-457.2, 1371.6) * mm});
            skLineSegment(sketch, "E16.32.0.2", {"start": v(-508, 1320.8) * mm, "end": v(-457.2, 1320.8) * mm});
            skLineSegment(sketch, "E16.32.0.3", {"start": v(-508, 1320.8) * mm, "end": v(-508, 1371.6) * mm});
            skLineSegment(sketch, "E16.32.1.0", {"start": v(-508, 1625.6) * mm, "end": v(-457.2, 1625.6) * mm});
            skLineSegment(sketch, "E16.32.1.1", {"start": v(-457.2, 1574.8) * mm, "end": v(-457.2, 1625.6) * mm});
            skLineSegment(sketch, "E16.32.1.2", {"start": v(-508, 1574.8) * mm, "end": v(-457.2, 1574.8) * mm});
            skLineSegment(sketch, "E16.32.1.3", {"start": v(-508, 1574.8) * mm, "end": v(-508, 1625.6) * mm});
            skLineSegment(sketch, "E16.33.0.0", {"start": v(-254, 1371.6) * mm, "end": v(-203.2, 1371.6) * mm});
            skLineSegment(sketch, "E16.33.0.1", {"start": v(-203.2, 1320.8) * mm, "end": v(-203.2, 1371.6) * mm});
            skLineSegment(sketch, "E16.33.0.2", {"start": v(-254, 1320.8) * mm, "end": v(-203.2, 1320.8) * mm});
            skLineSegment(sketch, "E16.33.0.3", {"start": v(-254, 1320.8) * mm, "end": v(-254, 1371.6) * mm});
            skLineSegment(sketch, "E16.33.1.0", {"start": v(-254, 1625.6) * mm, "end": v(-203.2, 1625.6) * mm});
            skLineSegment(sketch, "E16.33.1.1", {"start": v(-203.2, 1574.8) * mm, "end": v(-203.2, 1625.6) * mm});
            skLineSegment(sketch, "E16.33.1.2", {"start": v(-254, 1574.8) * mm, "end": v(-203.2, 1574.8) * mm});
            skLineSegment(sketch, "E16.33.1.3", {"start": v(-254, 1574.8) * mm, "end": v(-254, 1625.6) * mm});
            skLineSegment(sketch, "E16.direction1", {"start": v(-8636, 1371.6) * mm, "end": v(-8382, 1371.6) * mm, "construction": true});
            skLineSegment(sketch, "E16.direction2", {"start": v(-8636, 1371.6) * mm, "end": v(-8636, 1625.6) * mm, "construction": true});
            skSolve(sketch);
        }
        {
            var Q0;
            Q0 = qSketchRegion(id + "F5", true);
            var Q1;
            Q1=makeQuery(id+"F1.opExtrude","SWEPT_BODY",BODY,{"disambiguationData":[OSD([sQuery(id+"F0.wireOp",EDGE,"E0"),sQuery(id+"F0.wireOp",EDGE,"E1"),sQuery(id+"F0.wireOp",EDGE,"E2"),sQuery(id+"F0.wireOp",EDGE,"E3"),sQuery(id+"F0.wireOp",EDGE,"E4")])]});
            var Q2;
            Q2=makeQuery(id+"F1.opExtrude","SWEPT_BODY",BODY,{"disambiguationData":[OSD([sQuery(id+"F0.wireOp",EDGE,"E0"),sQuery(id+"F0.wireOp",EDGE,"E1"),sQuery(id+"F0.wireOp",EDGE,"E2"),sQuery(id+"F0.wireOp",EDGE,"E3"),sQuery(id+"F0.wireOp",EDGE,"E4")])]});
            extrude(context, id + "F6", {"entities" : qUnion([Q0]), "operationType" : NewBodyOperationType.ADD, "endBound" : BoundingType.UP_TO_BODY, "endBoundEntityBody" : qUnion([Q1]), "depth" : 25.4 * mm, "hasSecondDirection" : true, "secondDirectionBound" : SecondDirectionBoundingType.UP_TO_BODY, "secondDirectionOppositeDirection" : true, "secondDirectionBoundEntityBody" : qUnion([Q2]), "secondDirectionDepth" : 25.4 * mm});
        }
        {
            var Q0;
            Q0=makeQuery(id+"F6.opExtrude","SWEPT_FACE",FACE,{"disambiguationData":[OSD([sQuery(id+"F5.wireOp",EDGE,"E16.0.1.2")])]});
            var sketch = newSketch(context, id + "F7", { "sketchPlane" : qUnion([Q0])});
            skLineSegment(sketch, "E17.bottom", {"start": v(-302.25, 8636) * mm, "end": v(-276.85, 8636) * mm});
            skLineSegment(sketch, "E17.top", {"start": v(-302.25, 8585.2) * mm, "end": v(-276.85, 8585.2) * mm});
            skLineSegment(sketch, "E17.left", {"start": v(-302.25, 8636) * mm, "end": v(-302.25, 8585.2) * mm});
            skLineSegment(sketch, "E17.right", {"start": v(-276.85, 8636) * mm, "end": v(-276.85, 8585.2) * mm});
            skLineSegment(sketch, "E18.bottom", {"start": v(276.85, 8636) * mm, "end": v(302.25, 8636) * mm});
            skLineSegment(sketch, "E18.top", {"start": v(276.85, 8585.2) * mm, "end": v(302.25, 8585.2) * mm});
            skLineSegment(sketch, "E18.left", {"start": v(276.85, 8636) * mm, "end": v(276.85, 8585.2) * mm});
            skLineSegment(sketch, "E18.right", {"start": v(302.25, 8636) * mm, "end": v(302.25, 8585.2) * mm});
            skLineSegment(sketch, "E19.0.1.0", {"start": v(-276.85, 8382) * mm, "end": v(-276.85, 8331.2) * mm});
            skLineSegment(sketch, "E19.0.1.1", {"start": v(-302.25, 8382) * mm, "end": v(-276.85, 8382) * mm});
            skLineSegment(sketch, "E19.0.1.2", {"start": v(-302.25, 8382) * mm, "end": v(-302.25, 8331.2) * mm});
            skLineSegment(sketch, "E19.0.1.3", {"start": v(-302.25, 8331.2) * mm, "end": v(-276.85, 8331.2) * mm});
            skLineSegment(sketch, "E19.0.1.4", {"start": v(302.25, 8382) * mm, "end": v(302.25, 8331.2) * mm});
            skLineSegment(sketch, "E19.0.1.5", {"start": v(276.85, 8382) * mm, "end": v(302.25, 8382) * mm});
            skLineSegment(sketch, "E19.0.1.6", {"start": v(276.85, 8382) * mm, "end": v(276.85, 8331.2) * mm});
            skLineSegment(sketch, "E19.0.1.7", {"start": v(276.85, 8331.2) * mm, "end": v(302.25, 8331.2) * mm});
            skLineSegment(sketch, "E19.0.2.0", {"start": v(-276.85, 8128) * mm, "end": v(-276.85, 8077.2) * mm});
            skLineSegment(sketch, "E19.0.2.1", {"start": v(-302.25, 8128) * mm, "end": v(-276.85, 8128) * mm});
            skLineSegment(sketch, "E19.0.2.2", {"start": v(-302.25, 8128) * mm, "end": v(-302.25, 8077.2) * mm});
            skLineSegment(sketch, "E19.0.2.3", {"start": v(-302.25, 8077.2) * mm, "end": v(-276.85, 8077.2) * mm});
            skLineSegment(sketch, "E19.0.2.4", {"start": v(302.25, 8128) * mm, "end": v(302.25, 8077.2) * mm});
            skLineSegment(sketch, "E19.0.2.5", {"start": v(276.85, 8128) * mm, "end": v(302.25, 8128) * mm});
            skLineSegment(sketch, "E19.0.2.6", {"start": v(276.85, 8128) * mm, "end": v(276.85, 8077.2) * mm});
            skLineSegment(sketch, "E19.0.2.7", {"start": v(276.85, 8077.2) * mm, "end": v(302.25, 8077.2) * mm});
            skLineSegment(sketch, "E19.0.3.0", {"start": v(-276.85, 7874) * mm, "end": v(-276.85, 7823.2) * mm});
            skLineSegment(sketch, "E19.0.3.1", {"start": v(-302.25, 7874) * mm, "end": v(-276.85, 7874) * mm});
            skLineSegment(sketch, "E19.0.3.2", {"start": v(-302.25, 7874) * mm, "end": v(-302.25, 7823.2) * mm});
            skLineSegment(sketch, "E19.0.3.3", {"start": v(-302.25, 7823.2) * mm, "end": v(-276.85, 7823.2) * mm});
            skLineSegment(sketch, "E19.0.3.4", {"start": v(302.25, 7874) * mm, "end": v(302.25, 7823.2) * mm});
            skLineSegment(sketch, "E19.0.3.5", {"start": v(276.85, 7874) * mm, "end": v(302.25, 7874) * mm});
            skLineSegment(sketch, "E19.0.3.6", {"start": v(276.85, 7874) * mm, "end": v(276.85, 7823.2) * mm});
            skLineSegment(sketch, "E19.0.3.7", {"start": v(276.85, 7823.2) * mm, "end": v(302.25, 7823.2) * mm});
            skLineSegment(sketch, "E19.0.4.0", {"start": v(-276.85, 7620) * mm, "end": v(-276.85, 7569.2) * mm});
            skLineSegment(sketch, "E19.0.4.1", {"start": v(-302.25, 7620) * mm, "end": v(-276.85, 7620) * mm});
            skLineSegment(sketch, "E19.0.4.2", {"start": v(-302.25, 7620) * mm, "end": v(-302.25, 7569.2) * mm});
            skLineSegment(sketch, "E19.0.4.3", {"start": v(-302.25, 7569.2) * mm, "end": v(-276.85, 7569.2) * mm});
            skLineSegment(sketch, "E19.0.4.4", {"start": v(302.25, 7620) * mm, "end": v(302.25, 7569.2) * mm});
            skLineSegment(sketch, "E19.0.4.5", {"start": v(276.85, 7620) * mm, "end": v(302.25, 7620) * mm});
            skLineSegment(sketch, "E19.0.4.6", {"start": v(276.85, 7620) * mm, "end": v(276.85, 7569.2) * mm});
            skLineSegment(sketch, "E19.0.4.7", {"start": v(276.85, 7569.2) * mm, "end": v(302.25, 7569.2) * mm});
            skLineSegment(sketch, "E19.0.5.0", {"start": v(-276.85, 7366) * mm, "end": v(-276.85, 7315.2) * mm});
            skLineSegment(sketch, "E19.0.5.1", {"start": v(-302.25, 7366) * mm, "end": v(-276.85, 7366) * mm});
            skLineSegment(sketch, "E19.0.5.2", {"start": v(-302.25, 7366) * mm, "end": v(-302.25, 7315.2) * mm});
            skLineSegment(sketch, "E19.0.5.3", {"start": v(-302.25, 7315.2) * mm, "end": v(-276.85, 7315.2) * mm});
            skLineSegment(sketch, "E19.0.5.4", {"start": v(302.25, 7366) * mm, "end": v(302.25, 7315.2) * mm});
            skLineSegment(sketch, "E19.0.5.5", {"start": v(276.85, 7366) * mm, "end": v(302.25, 7366) * mm});
            skLineSegment(sketch, "E19.0.5.6", {"start": v(276.85, 7366) * mm, "end": v(276.85, 7315.2) * mm});
            skLineSegment(sketch, "E19.0.5.7", {"start": v(276.85, 7315.2) * mm, "end": v(302.25, 7315.2) * mm});
            skLineSegment(sketch, "E19.0.6.0", {"start": v(-276.85, 7112) * mm, "end": v(-276.85, 7061.2) * mm});
            skLineSegment(sketch, "E19.0.6.1", {"start": v(-302.25, 7112) * mm, "end": v(-276.85, 7112) * mm});
            skLineSegment(sketch, "E19.0.6.2", {"start": v(-302.25, 7112) * mm, "end": v(-302.25, 7061.2) * mm});
            skLineSegment(sketch, "E19.0.6.3", {"start": v(-302.25, 7061.2) * mm, "end": v(-276.85, 7061.2) * mm});
            skLineSegment(sketch, "E19.0.6.4", {"start": v(302.25, 7112) * mm, "end": v(302.25, 7061.2) * mm});
            skLineSegment(sketch, "E19.0.6.5", {"start": v(276.85, 7112) * mm, "end": v(302.25, 7112) * mm});
            skLineSegment(sketch, "E19.0.6.6", {"start": v(276.85, 7112) * mm, "end": v(276.85, 7061.2) * mm});
            skLineSegment(sketch, "E19.0.6.7", {"start": v(276.85, 7061.2) * mm, "end": v(302.25, 7061.2) * mm});
            skLineSegment(sketch, "E19.0.7.0", {"start": v(-276.85, 6858) * mm, "end": v(-276.85, 6807.2) * mm});
            skLineSegment(sketch, "E19.0.7.1", {"start": v(-302.25, 6858) * mm, "end": v(-276.85, 6858) * mm});
            skLineSegment(sketch, "E19.0.7.2", {"start": v(-302.25, 6858) * mm, "end": v(-302.25, 6807.2) * mm});
            skLineSegment(sketch, "E19.0.7.3", {"start": v(-302.25, 6807.2) * mm, "end": v(-276.85, 6807.2) * mm});
            skLineSegment(sketch, "E19.0.7.4", {"start": v(302.25, 6858) * mm, "end": v(302.25, 6807.2) * mm});
            skLineSegment(sketch, "E19.0.7.5", {"start": v(276.85, 6858) * mm, "end": v(302.25, 6858) * mm});
            skLineSegment(sketch, "E19.0.7.6", {"start": v(276.85, 6858) * mm, "end": v(276.85, 6807.2) * mm});
            skLineSegment(sketch, "E19.0.7.7", {"start": v(276.85, 6807.2) * mm, "end": v(302.25, 6807.2) * mm});
            skLineSegment(sketch, "E19.0.8.0", {"start": v(-276.85, 6604) * mm, "end": v(-276.85, 6553.2) * mm});
            skLineSegment(sketch, "E19.0.8.1", {"start": v(-302.25, 6604) * mm, "end": v(-276.85, 6604) * mm});
            skLineSegment(sketch, "E19.0.8.2", {"start": v(-302.25, 6604) * mm, "end": v(-302.25, 6553.2) * mm});
            skLineSegment(sketch, "E19.0.8.3", {"start": v(-302.25, 6553.2) * mm, "end": v(-276.85, 6553.2) * mm});
            skLineSegment(sketch, "E19.0.8.4", {"start": v(302.25, 6604) * mm, "end": v(302.25, 6553.2) * mm});
            skLineSegment(sketch, "E19.0.8.5", {"start": v(276.85, 6604) * mm, "end": v(302.25, 6604) * mm});
            skLineSegment(sketch, "E19.0.8.6", {"start": v(276.85, 6604) * mm, "end": v(276.85, 6553.2) * mm});
            skLineSegment(sketch, "E19.0.8.7", {"start": v(276.85, 6553.2) * mm, "end": v(302.25, 6553.2) * mm});
            skLineSegment(sketch, "E19.0.9.0", {"start": v(-276.85, 6350) * mm, "end": v(-276.85, 6299.2) * mm});
            skLineSegment(sketch, "E19.0.9.1", {"start": v(-302.25, 6350) * mm, "end": v(-276.85, 6350) * mm});
            skLineSegment(sketch, "E19.0.9.2", {"start": v(-302.25, 6350) * mm, "end": v(-302.25, 6299.2) * mm});
            skLineSegment(sketch, "E19.0.9.3", {"start": v(-302.25, 6299.2) * mm, "end": v(-276.85, 6299.2) * mm});
            skLineSegment(sketch, "E19.0.9.4", {"start": v(302.25, 6350) * mm, "end": v(302.25, 6299.2) * mm});
            skLineSegment(sketch, "E19.0.9.5", {"start": v(276.85, 6350) * mm, "end": v(302.25, 6350) * mm});
            skLineSegment(sketch, "E19.0.9.6", {"start": v(276.85, 6350) * mm, "end": v(276.85, 6299.2) * mm});
            skLineSegment(sketch, "E19.0.9.7", {"start": v(276.85, 6299.2) * mm, "end": v(302.25, 6299.2) * mm});
            skLineSegment(sketch, "E19.0.10.0", {"start": v(-276.85, 6096) * mm, "end": v(-276.85, 6045.2) * mm});
            skLineSegment(sketch, "E19.0.10.1", {"start": v(-302.25, 6096) * mm, "end": v(-276.85, 6096) * mm});
            skLineSegment(sketch, "E19.0.10.2", {"start": v(-302.25, 6096) * mm, "end": v(-302.25, 6045.2) * mm});
            skLineSegment(sketch, "E19.0.10.3", {"start": v(-302.25, 6045.2) * mm, "end": v(-276.85, 6045.2) * mm});
            skLineSegment(sketch, "E19.0.10.4", {"start": v(302.25, 6096) * mm, "end": v(302.25, 6045.2) * mm});
            skLineSegment(sketch, "E19.0.10.5", {"start": v(276.85, 6096) * mm, "end": v(302.25, 6096) * mm});
            skLineSegment(sketch, "E19.0.10.6", {"start": v(276.85, 6096) * mm, "end": v(276.85, 6045.2) * mm});
            skLineSegment(sketch, "E19.0.10.7", {"start": v(276.85, 6045.2) * mm, "end": v(302.25, 6045.2) * mm});
            skLineSegment(sketch, "E19.0.11.0", {"start": v(-276.85, 5842) * mm, "end": v(-276.85, 5791.2) * mm});
            skLineSegment(sketch, "E19.0.11.1", {"start": v(-302.25, 5842) * mm, "end": v(-276.85, 5842) * mm});
            skLineSegment(sketch, "E19.0.11.2", {"start": v(-302.25, 5842) * mm, "end": v(-302.25, 5791.2) * mm});
            skLineSegment(sketch, "E19.0.11.3", {"start": v(-302.25, 5791.2) * mm, "end": v(-276.85, 5791.2) * mm});
            skLineSegment(sketch, "E19.0.11.4", {"start": v(302.25, 5842) * mm, "end": v(302.25, 5791.2) * mm});
            skLineSegment(sketch, "E19.0.11.5", {"start": v(276.85, 5842) * mm, "end": v(302.25, 5842) * mm});
            skLineSegment(sketch, "E19.0.11.6", {"start": v(276.85, 5842) * mm, "end": v(276.85, 5791.2) * mm});
            skLineSegment(sketch, "E19.0.11.7", {"start": v(276.85, 5791.2) * mm, "end": v(302.25, 5791.2) * mm});
            skLineSegment(sketch, "E19.0.12.0", {"start": v(-276.85, 5588) * mm, "end": v(-276.85, 5537.2) * mm});
            skLineSegment(sketch, "E19.0.12.1", {"start": v(-302.25, 5588) * mm, "end": v(-276.85, 5588) * mm});
            skLineSegment(sketch, "E19.0.12.2", {"start": v(-302.25, 5588) * mm, "end": v(-302.25, 5537.2) * mm});
            skLineSegment(sketch, "E19.0.12.3", {"start": v(-302.25, 5537.2) * mm, "end": v(-276.85, 5537.2) * mm});
            skLineSegment(sketch, "E19.0.12.4", {"start": v(302.25, 5588) * mm, "end": v(302.25, 5537.2) * mm});
            skLineSegment(sketch, "E19.0.12.5", {"start": v(276.85, 5588) * mm, "end": v(302.25, 5588) * mm});
            skLineSegment(sketch, "E19.0.12.6", {"start": v(276.85, 5588) * mm, "end": v(276.85, 5537.2) * mm});
            skLineSegment(sketch, "E19.0.12.7", {"start": v(276.85, 5537.2) * mm, "end": v(302.25, 5537.2) * mm});
            skLineSegment(sketch, "E19.0.13.0", {"start": v(-276.85, 5334) * mm, "end": v(-276.85, 5283.2) * mm});
            skLineSegment(sketch, "E19.0.13.1", {"start": v(-302.25, 5334) * mm, "end": v(-276.85, 5334) * mm});
            skLineSegment(sketch, "E19.0.13.2", {"start": v(-302.25, 5334) * mm, "end": v(-302.25, 5283.2) * mm});
            skLineSegment(sketch, "E19.0.13.3", {"start": v(-302.25, 5283.2) * mm, "end": v(-276.85, 5283.2) * mm});
            skLineSegment(sketch, "E19.0.13.4", {"start": v(302.25, 5334) * mm, "end": v(302.25, 5283.2) * mm});
            skLineSegment(sketch, "E19.0.13.5", {"start": v(276.85, 5334) * mm, "end": v(302.25, 5334) * mm});
            skLineSegment(sketch, "E19.0.13.6", {"start": v(276.85, 5334) * mm, "end": v(276.85, 5283.2) * mm});
            skLineSegment(sketch, "E19.0.13.7", {"start": v(276.85, 5283.2) * mm, "end": v(302.25, 5283.2) * mm});
            skLineSegment(sketch, "E19.0.14.0", {"start": v(-276.85, 5080) * mm, "end": v(-276.85, 5029.2) * mm});
            skLineSegment(sketch, "E19.0.14.1", {"start": v(-302.25, 5080) * mm, "end": v(-276.85, 5080) * mm});
            skLineSegment(sketch, "E19.0.14.2", {"start": v(-302.25, 5080) * mm, "end": v(-302.25, 5029.2) * mm});
            skLineSegment(sketch, "E19.0.14.3", {"start": v(-302.25, 5029.2) * mm, "end": v(-276.85, 5029.2) * mm});
            skLineSegment(sketch, "E19.0.14.4", {"start": v(302.25, 5080) * mm, "end": v(302.25, 5029.2) * mm});
            skLineSegment(sketch, "E19.0.14.5", {"start": v(276.85, 5080) * mm, "end": v(302.25, 5080) * mm});
            skLineSegment(sketch, "E19.0.14.6", {"start": v(276.85, 5080) * mm, "end": v(276.85, 5029.2) * mm});
            skLineSegment(sketch, "E19.0.14.7", {"start": v(276.85, 5029.2) * mm, "end": v(302.25, 5029.2) * mm});
            skLineSegment(sketch, "E19.0.15.0", {"start": v(-276.85, 4826) * mm, "end": v(-276.85, 4775.2) * mm});
            skLineSegment(sketch, "E19.0.15.1", {"start": v(-302.25, 4826) * mm, "end": v(-276.85, 4826) * mm});
            skLineSegment(sketch, "E19.0.15.2", {"start": v(-302.25, 4826) * mm, "end": v(-302.25, 4775.2) * mm});
            skLineSegment(sketch, "E19.0.15.3", {"start": v(-302.25, 4775.2) * mm, "end": v(-276.85, 4775.2) * mm});
            skLineSegment(sketch, "E19.0.15.4", {"start": v(302.25, 4826) * mm, "end": v(302.25, 4775.2) * mm});
            skLineSegment(sketch, "E19.0.15.5", {"start": v(276.85, 4826) * mm, "end": v(302.25, 4826) * mm});
            skLineSegment(sketch, "E19.0.15.6", {"start": v(276.85, 4826) * mm, "end": v(276.85, 4775.2) * mm});
            skLineSegment(sketch, "E19.0.15.7", {"start": v(276.85, 4775.2) * mm, "end": v(302.25, 4775.2) * mm});
            skLineSegment(sketch, "E19.0.16.0", {"start": v(-276.85, 4572) * mm, "end": v(-276.85, 4521.2) * mm});
            skLineSegment(sketch, "E19.0.16.1", {"start": v(-302.25, 4572) * mm, "end": v(-276.85, 4572) * mm});
            skLineSegment(sketch, "E19.0.16.2", {"start": v(-302.25, 4572) * mm, "end": v(-302.25, 4521.2) * mm});
            skLineSegment(sketch, "E19.0.16.3", {"start": v(-302.25, 4521.2) * mm, "end": v(-276.85, 4521.2) * mm});
            skLineSegment(sketch, "E19.0.16.4", {"start": v(302.25, 4572) * mm, "end": v(302.25, 4521.2) * mm});
            skLineSegment(sketch, "E19.0.16.5", {"start": v(276.85, 4572) * mm, "end": v(302.25, 4572) * mm});
            skLineSegment(sketch, "E19.0.16.6", {"start": v(276.85, 4572) * mm, "end": v(276.85, 4521.2) * mm});
            skLineSegment(sketch, "E19.0.16.7", {"start": v(276.85, 4521.2) * mm, "end": v(302.25, 4521.2) * mm});
            skLineSegment(sketch, "E19.0.17.0", {"start": v(-276.85, 4318) * mm, "end": v(-276.85, 4267.2) * mm});
            skLineSegment(sketch, "E19.0.17.1", {"start": v(-302.25, 4318) * mm, "end": v(-276.85, 4318) * mm});
            skLineSegment(sketch, "E19.0.17.2", {"start": v(-302.25, 4318) * mm, "end": v(-302.25, 4267.2) * mm});
            skLineSegment(sketch, "E19.0.17.3", {"start": v(-302.25, 4267.2) * mm, "end": v(-276.85, 4267.2) * mm});
            skLineSegment(sketch, "E19.0.17.4", {"start": v(302.25, 4318) * mm, "end": v(302.25, 4267.2) * mm});
            skLineSegment(sketch, "E19.0.17.5", {"start": v(276.85, 4318) * mm, "end": v(302.25, 4318) * mm});
            skLineSegment(sketch, "E19.0.17.6", {"start": v(276.85, 4318) * mm, "end": v(276.85, 4267.2) * mm});
            skLineSegment(sketch, "E19.0.17.7", {"start": v(276.85, 4267.2) * mm, "end": v(302.25, 4267.2) * mm});
            skLineSegment(sketch, "E19.0.18.0", {"start": v(-276.85, 4064) * mm, "end": v(-276.85, 4013.2) * mm});
            skLineSegment(sketch, "E19.0.18.1", {"start": v(-302.25, 4064) * mm, "end": v(-276.85, 4064) * mm});
            skLineSegment(sketch, "E19.0.18.2", {"start": v(-302.25, 4064) * mm, "end": v(-302.25, 4013.2) * mm});
            skLineSegment(sketch, "E19.0.18.3", {"start": v(-302.25, 4013.2) * mm, "end": v(-276.85, 4013.2) * mm});
            skLineSegment(sketch, "E19.0.18.4", {"start": v(302.25, 4064) * mm, "end": v(302.25, 4013.2) * mm});
            skLineSegment(sketch, "E19.0.18.5", {"start": v(276.85, 4064) * mm, "end": v(302.25, 4064) * mm});
            skLineSegment(sketch, "E19.0.18.6", {"start": v(276.85, 4064) * mm, "end": v(276.85, 4013.2) * mm});
            skLineSegment(sketch, "E19.0.18.7", {"start": v(276.85, 4013.2) * mm, "end": v(302.25, 4013.2) * mm});
            skLineSegment(sketch, "E19.0.19.0", {"start": v(-276.85, 3810) * mm, "end": v(-276.85, 3759.2) * mm});
            skLineSegment(sketch, "E19.0.19.1", {"start": v(-302.25, 3810) * mm, "end": v(-276.85, 3810) * mm});
            skLineSegment(sketch, "E19.0.19.2", {"start": v(-302.25, 3810) * mm, "end": v(-302.25, 3759.2) * mm});
            skLineSegment(sketch, "E19.0.19.3", {"start": v(-302.25, 3759.2) * mm, "end": v(-276.85, 3759.2) * mm});
            skLineSegment(sketch, "E19.0.19.4", {"start": v(302.25, 3810) * mm, "end": v(302.25, 3759.2) * mm});
            skLineSegment(sketch, "E19.0.19.5", {"start": v(276.85, 3810) * mm, "end": v(302.25, 3810) * mm});
            skLineSegment(sketch, "E19.0.19.6", {"start": v(276.85, 3810) * mm, "end": v(276.85, 3759.2) * mm});
            skLineSegment(sketch, "E19.0.19.7", {"start": v(276.85, 3759.2) * mm, "end": v(302.25, 3759.2) * mm});
            skLineSegment(sketch, "E19.0.20.0", {"start": v(-276.85, 3556) * mm, "end": v(-276.85, 3505.2) * mm});
            skLineSegment(sketch, "E19.0.20.1", {"start": v(-302.25, 3556) * mm, "end": v(-276.85, 3556) * mm});
            skLineSegment(sketch, "E19.0.20.2", {"start": v(-302.25, 3556) * mm, "end": v(-302.25, 3505.2) * mm});
            skLineSegment(sketch, "E19.0.20.3", {"start": v(-302.25, 3505.2) * mm, "end": v(-276.85, 3505.2) * mm});
            skLineSegment(sketch, "E19.0.20.4", {"start": v(302.25, 3556) * mm, "end": v(302.25, 3505.2) * mm});
            skLineSegment(sketch, "E19.0.20.5", {"start": v(276.85, 3556) * mm, "end": v(302.25, 3556) * mm});
            skLineSegment(sketch, "E19.0.20.6", {"start": v(276.85, 3556) * mm, "end": v(276.85, 3505.2) * mm});
            skLineSegment(sketch, "E19.0.20.7", {"start": v(276.85, 3505.2) * mm, "end": v(302.25, 3505.2) * mm});
            skLineSegment(sketch, "E19.0.21.0", {"start": v(-276.85, 3302) * mm, "end": v(-276.85, 3251.2) * mm});
            skLineSegment(sketch, "E19.0.21.1", {"start": v(-302.25, 3302) * mm, "end": v(-276.85, 3302) * mm});
            skLineSegment(sketch, "E19.0.21.2", {"start": v(-302.25, 3302) * mm, "end": v(-302.25, 3251.2) * mm});
            skLineSegment(sketch, "E19.0.21.3", {"start": v(-302.25, 3251.2) * mm, "end": v(-276.85, 3251.2) * mm});
            skLineSegment(sketch, "E19.0.21.4", {"start": v(302.25, 3302) * mm, "end": v(302.25, 3251.2) * mm});
            skLineSegment(sketch, "E19.0.21.5", {"start": v(276.85, 3302) * mm, "end": v(302.25, 3302) * mm});
            skLineSegment(sketch, "E19.0.21.6", {"start": v(276.85, 3302) * mm, "end": v(276.85, 3251.2) * mm});
            skLineSegment(sketch, "E19.0.21.7", {"start": v(276.85, 3251.2) * mm, "end": v(302.25, 3251.2) * mm});
            skLineSegment(sketch, "E19.0.22.0", {"start": v(-276.85, 3048) * mm, "end": v(-276.85, 2997.2) * mm});
            skLineSegment(sketch, "E19.0.22.1", {"start": v(-302.25, 3048) * mm, "end": v(-276.85, 3048) * mm});
            skLineSegment(sketch, "E19.0.22.2", {"start": v(-302.25, 3048) * mm, "end": v(-302.25, 2997.2) * mm});
            skLineSegment(sketch, "E19.0.22.3", {"start": v(-302.25, 2997.2) * mm, "end": v(-276.85, 2997.2) * mm});
            skLineSegment(sketch, "E19.0.22.4", {"start": v(302.25, 3048) * mm, "end": v(302.25, 2997.2) * mm});
            skLineSegment(sketch, "E19.0.22.5", {"start": v(276.85, 3048) * mm, "end": v(302.25, 3048) * mm});
            skLineSegment(sketch, "E19.0.22.6", {"start": v(276.85, 3048) * mm, "end": v(276.85, 2997.2) * mm});
            skLineSegment(sketch, "E19.0.22.7", {"start": v(276.85, 2997.2) * mm, "end": v(302.25, 2997.2) * mm});
            skLineSegment(sketch, "E19.0.23.0", {"start": v(-276.85, 2794) * mm, "end": v(-276.85, 2743.2) * mm});
            skLineSegment(sketch, "E19.0.23.1", {"start": v(-302.25, 2794) * mm, "end": v(-276.85, 2794) * mm});
            skLineSegment(sketch, "E19.0.23.2", {"start": v(-302.25, 2794) * mm, "end": v(-302.25, 2743.2) * mm});
            skLineSegment(sketch, "E19.0.23.3", {"start": v(-302.25, 2743.2) * mm, "end": v(-276.85, 2743.2) * mm});
            skLineSegment(sketch, "E19.0.23.4", {"start": v(302.25, 2794) * mm, "end": v(302.25, 2743.2) * mm});
            skLineSegment(sketch, "E19.0.23.5", {"start": v(276.85, 2794) * mm, "end": v(302.25, 2794) * mm});
            skLineSegment(sketch, "E19.0.23.6", {"start": v(276.85, 2794) * mm, "end": v(276.85, 2743.2) * mm});
            skLineSegment(sketch, "E19.0.23.7", {"start": v(276.85, 2743.2) * mm, "end": v(302.25, 2743.2) * mm});
            skLineSegment(sketch, "E19.0.24.0", {"start": v(-276.85, 2540) * mm, "end": v(-276.85, 2489.2) * mm});
            skLineSegment(sketch, "E19.0.24.1", {"start": v(-302.25, 2540) * mm, "end": v(-276.85, 2540) * mm});
            skLineSegment(sketch, "E19.0.24.2", {"start": v(-302.25, 2540) * mm, "end": v(-302.25, 2489.2) * mm});
            skLineSegment(sketch, "E19.0.24.3", {"start": v(-302.25, 2489.2) * mm, "end": v(-276.85, 2489.2) * mm});
            skLineSegment(sketch, "E19.0.24.4", {"start": v(302.25, 2540) * mm, "end": v(302.25, 2489.2) * mm});
            skLineSegment(sketch, "E19.0.24.5", {"start": v(276.85, 2540) * mm, "end": v(302.25, 2540) * mm});
            skLineSegment(sketch, "E19.0.24.6", {"start": v(276.85, 2540) * mm, "end": v(276.85, 2489.2) * mm});
            skLineSegment(sketch, "E19.0.24.7", {"start": v(276.85, 2489.2) * mm, "end": v(302.25, 2489.2) * mm});
            skLineSegment(sketch, "E19.0.25.0", {"start": v(-276.85, 2286) * mm, "end": v(-276.85, 2235.2) * mm});
            skLineSegment(sketch, "E19.0.25.1", {"start": v(-302.25, 2286) * mm, "end": v(-276.85, 2286) * mm});
            skLineSegment(sketch, "E19.0.25.2", {"start": v(-302.25, 2286) * mm, "end": v(-302.25, 2235.2) * mm});
            skLineSegment(sketch, "E19.0.25.3", {"start": v(-302.25, 2235.2) * mm, "end": v(-276.85, 2235.2) * mm});
            skLineSegment(sketch, "E19.0.25.4", {"start": v(302.25, 2286) * mm, "end": v(302.25, 2235.2) * mm});
            skLineSegment(sketch, "E19.0.25.5", {"start": v(276.85, 2286) * mm, "end": v(302.25, 2286) * mm});
            skLineSegment(sketch, "E19.0.25.6", {"start": v(276.85, 2286) * mm, "end": v(276.85, 2235.2) * mm});
            skLineSegment(sketch, "E19.0.25.7", {"start": v(276.85, 2235.2) * mm, "end": v(302.25, 2235.2) * mm});
            skLineSegment(sketch, "E19.0.26.0", {"start": v(-276.85, 2032) * mm, "end": v(-276.85, 1981.2) * mm});
            skLineSegment(sketch, "E19.0.26.1", {"start": v(-302.25, 2032) * mm, "end": v(-276.85, 2032) * mm});
            skLineSegment(sketch, "E19.0.26.2", {"start": v(-302.25, 2032) * mm, "end": v(-302.25, 1981.2) * mm});
            skLineSegment(sketch, "E19.0.26.3", {"start": v(-302.25, 1981.2) * mm, "end": v(-276.85, 1981.2) * mm});
            skLineSegment(sketch, "E19.0.26.4", {"start": v(302.25, 2032) * mm, "end": v(302.25, 1981.2) * mm});
            skLineSegment(sketch, "E19.0.26.5", {"start": v(276.85, 2032) * mm, "end": v(302.25, 2032) * mm});
            skLineSegment(sketch, "E19.0.26.6", {"start": v(276.85, 2032) * mm, "end": v(276.85, 1981.2) * mm});
            skLineSegment(sketch, "E19.0.26.7", {"start": v(276.85, 1981.2) * mm, "end": v(302.25, 1981.2) * mm});
            skLineSegment(sketch, "E19.0.27.0", {"start": v(-276.85, 1778) * mm, "end": v(-276.85, 1727.2) * mm});
            skLineSegment(sketch, "E19.0.27.1", {"start": v(-302.25, 1778) * mm, "end": v(-276.85, 1778) * mm});
            skLineSegment(sketch, "E19.0.27.2", {"start": v(-302.25, 1778) * mm, "end": v(-302.25, 1727.2) * mm});
            skLineSegment(sketch, "E19.0.27.3", {"start": v(-302.25, 1727.2) * mm, "end": v(-276.85, 1727.2) * mm});
            skLineSegment(sketch, "E19.0.27.4", {"start": v(302.25, 1778) * mm, "end": v(302.25, 1727.2) * mm});
            skLineSegment(sketch, "E19.0.27.5", {"start": v(276.85, 1778) * mm, "end": v(302.25, 1778) * mm});
            skLineSegment(sketch, "E19.0.27.6", {"start": v(276.85, 1778) * mm, "end": v(276.85, 1727.2) * mm});
            skLineSegment(sketch, "E19.0.27.7", {"start": v(276.85, 1727.2) * mm, "end": v(302.25, 1727.2) * mm});
            skLineSegment(sketch, "E19.0.28.0", {"start": v(-276.85, 1524) * mm, "end": v(-276.85, 1473.2) * mm});
            skLineSegment(sketch, "E19.0.28.1", {"start": v(-302.25, 1524) * mm, "end": v(-276.85, 1524) * mm});
            skLineSegment(sketch, "E19.0.28.2", {"start": v(-302.25, 1524) * mm, "end": v(-302.25, 1473.2) * mm});
            skLineSegment(sketch, "E19.0.28.3", {"start": v(-302.25, 1473.2) * mm, "end": v(-276.85, 1473.2) * mm});
            skLineSegment(sketch, "E19.0.28.4", {"start": v(302.25, 1524) * mm, "end": v(302.25, 1473.2) * mm});
            skLineSegment(sketch, "E19.0.28.5", {"start": v(276.85, 1524) * mm, "end": v(302.25, 1524) * mm});
            skLineSegment(sketch, "E19.0.28.6", {"start": v(276.85, 1524) * mm, "end": v(276.85, 1473.2) * mm});
            skLineSegment(sketch, "E19.0.28.7", {"start": v(276.85, 1473.2) * mm, "end": v(302.25, 1473.2) * mm});
            skLineSegment(sketch, "E19.0.29.0", {"start": v(-276.85, 1270) * mm, "end": v(-276.85, 1219.2) * mm});
            skLineSegment(sketch, "E19.0.29.1", {"start": v(-302.25, 1270) * mm, "end": v(-276.85, 1270) * mm});
            skLineSegment(sketch, "E19.0.29.2", {"start": v(-302.25, 1270) * mm, "end": v(-302.25, 1219.2) * mm});
            skLineSegment(sketch, "E19.0.29.3", {"start": v(-302.25, 1219.2) * mm, "end": v(-276.85, 1219.2) * mm});
            skLineSegment(sketch, "E19.0.29.4", {"start": v(302.25, 1270) * mm, "end": v(302.25, 1219.2) * mm});
            skLineSegment(sketch, "E19.0.29.5", {"start": v(276.85, 1270) * mm, "end": v(302.25, 1270) * mm});
            skLineSegment(sketch, "E19.0.29.6", {"start": v(276.85, 1270) * mm, "end": v(276.85, 1219.2) * mm});
            skLineSegment(sketch, "E19.0.29.7", {"start": v(276.85, 1219.2) * mm, "end": v(302.25, 1219.2) * mm});
            skLineSegment(sketch, "E19.0.30.0", {"start": v(-276.85, 1016) * mm, "end": v(-276.85, 965.2) * mm});
            skLineSegment(sketch, "E19.0.30.1", {"start": v(-302.25, 1016) * mm, "end": v(-276.85, 1016) * mm});
            skLineSegment(sketch, "E19.0.30.2", {"start": v(-302.25, 1016) * mm, "end": v(-302.25, 965.2) * mm});
            skLineSegment(sketch, "E19.0.30.3", {"start": v(-302.25, 965.2) * mm, "end": v(-276.85, 965.2) * mm});
            skLineSegment(sketch, "E19.0.30.4", {"start": v(302.25, 1016) * mm, "end": v(302.25, 965.2) * mm});
            skLineSegment(sketch, "E19.0.30.5", {"start": v(276.85, 1016) * mm, "end": v(302.25, 1016) * mm});
            skLineSegment(sketch, "E19.0.30.6", {"start": v(276.85, 1016) * mm, "end": v(276.85, 965.2) * mm});
            skLineSegment(sketch, "E19.0.30.7", {"start": v(276.85, 965.2) * mm, "end": v(302.25, 965.2) * mm});
            skLineSegment(sketch, "E19.0.31.0", {"start": v(-276.85, 762) * mm, "end": v(-276.85, 711.2) * mm});
            skLineSegment(sketch, "E19.0.31.1", {"start": v(-302.25, 762) * mm, "end": v(-276.85, 762) * mm});
            skLineSegment(sketch, "E19.0.31.2", {"start": v(-302.25, 762) * mm, "end": v(-302.25, 711.2) * mm});
            skLineSegment(sketch, "E19.0.31.3", {"start": v(-302.25, 711.2) * mm, "end": v(-276.85, 711.2) * mm});
            skLineSegment(sketch, "E19.0.31.4", {"start": v(302.25, 762) * mm, "end": v(302.25, 711.2) * mm});
            skLineSegment(sketch, "E19.0.31.5", {"start": v(276.85, 762) * mm, "end": v(302.25, 762) * mm});
            skLineSegment(sketch, "E19.0.31.6", {"start": v(276.85, 762) * mm, "end": v(276.85, 711.2) * mm});
            skLineSegment(sketch, "E19.0.31.7", {"start": v(276.85, 711.2) * mm, "end": v(302.25, 711.2) * mm});
            skLineSegment(sketch, "E19.0.32.0", {"start": v(-276.85, 508) * mm, "end": v(-276.85, 457.2) * mm});
            skLineSegment(sketch, "E19.0.32.1", {"start": v(-302.25, 508) * mm, "end": v(-276.85, 508) * mm});
            skLineSegment(sketch, "E19.0.32.2", {"start": v(-302.25, 508) * mm, "end": v(-302.25, 457.2) * mm});
            skLineSegment(sketch, "E19.0.32.3", {"start": v(-302.25, 457.2) * mm, "end": v(-276.85, 457.2) * mm});
            skLineSegment(sketch, "E19.0.32.4", {"start": v(302.25, 508) * mm, "end": v(302.25, 457.2) * mm});
            skLineSegment(sketch, "E19.0.32.5", {"start": v(276.85, 508) * mm, "end": v(302.25, 508) * mm});
            skLineSegment(sketch, "E19.0.32.6", {"start": v(276.85, 508) * mm, "end": v(276.85, 457.2) * mm});
            skLineSegment(sketch, "E19.0.32.7", {"start": v(276.85, 457.2) * mm, "end": v(302.25, 457.2) * mm});
            skLineSegment(sketch, "E19.0.33.0", {"start": v(-276.85, 254) * mm, "end": v(-276.85, 203.2) * mm});
            skLineSegment(sketch, "E19.0.33.1", {"start": v(-302.25, 254) * mm, "end": v(-276.85, 254) * mm});
            skLineSegment(sketch, "E19.0.33.2", {"start": v(-302.25, 254) * mm, "end": v(-302.25, 203.2) * mm});
            skLineSegment(sketch, "E19.0.33.3", {"start": v(-302.25, 203.2) * mm, "end": v(-276.85, 203.2) * mm});
            skLineSegment(sketch, "E19.0.33.4", {"start": v(302.25, 254) * mm, "end": v(302.25, 203.2) * mm});
            skLineSegment(sketch, "E19.0.33.5", {"start": v(276.85, 254) * mm, "end": v(302.25, 254) * mm});
            skLineSegment(sketch, "E19.0.33.6", {"start": v(276.85, 254) * mm, "end": v(276.85, 203.2) * mm});
            skLineSegment(sketch, "E19.0.33.7", {"start": v(276.85, 203.2) * mm, "end": v(302.25, 203.2) * mm});
            skLineSegment(sketch, "E19.direction1", {"start": v(-276.85, 8585.2) * mm, "end": v(-251.45, 8585.2) * mm, "construction": true});
            skLineSegment(sketch, "E19.direction2", {"start": v(-276.85, 8585.2) * mm, "end": v(-276.85, 8331.2) * mm, "construction": true});
            skSolve(sketch);
        }
        {
            var Q0;
            Q0 = qSketchRegion(id + "F7", true);
            var Q1;
            Q1=makeQuery(id+"F6.opExtrude","SWEPT_FACE",FACE,{"disambiguationData":[OSD([sQuery(id+"F5.wireOp",EDGE,"E15.top")])]});
            extrude(context, id + "F8", {"entities" : qUnion([Q0]), "operationType" : NewBodyOperationType.ADD, "endBound" : BoundingType.UP_TO_SURFACE, "endBoundEntityFace" : qUnion([Q1]), "depth" : 25.4 * mm});
        }
    });
